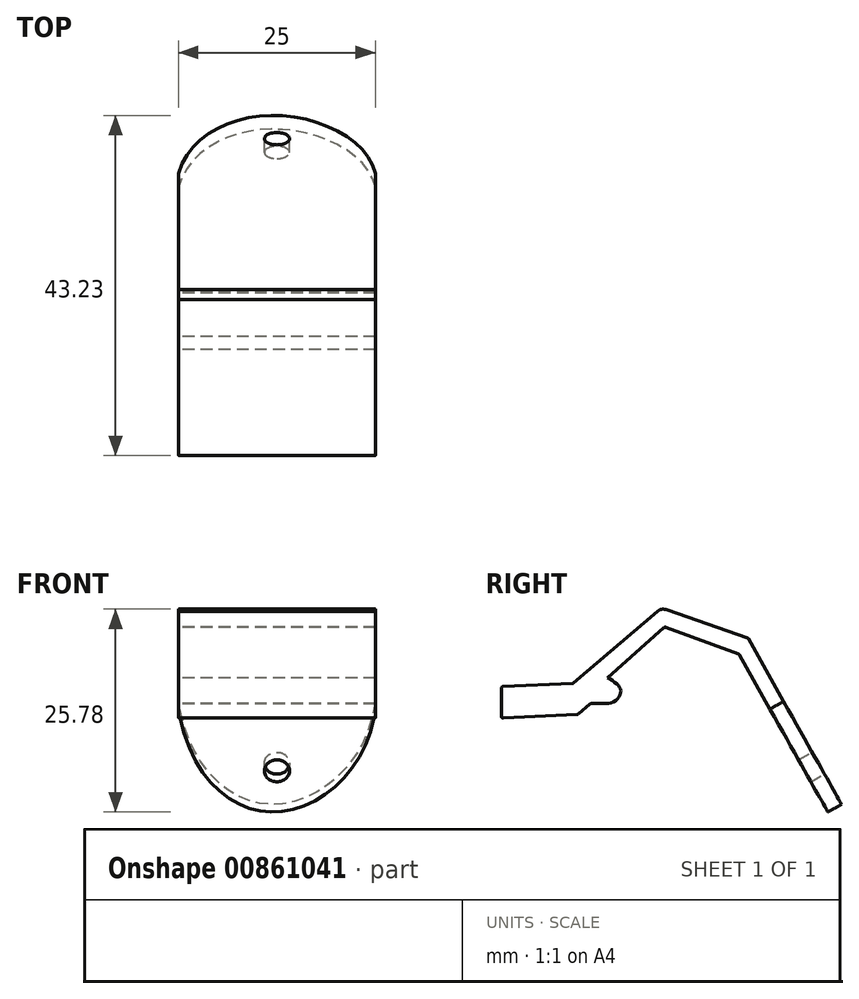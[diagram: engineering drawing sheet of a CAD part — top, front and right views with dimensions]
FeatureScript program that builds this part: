
annotation { "Feature Type Name" : "Feature", "Feature Type Description" : "" }
export const myFeature = defineFeature(function(context is Context, id is Id, definition is map)
    precondition{}
    {
        {
            var Q0;
            Q0=qCreatedBy(makeId("Right.planeOp"),FACE);
            var sketch = newSketch(context, id + "F0", { "sketchPlane" : qUnion([Q0])});
            skLineSegment(sketch, "E0", {"start": v(-12.97, -2.17) * mm, "end": v(-2.3, 6.93) * mm});
            skLineSegment(sketch, "E1", {"start": v(-1.03, 7.12) * mm, "end": v(9.1, 3.58) * mm});
            skLineSegment(sketch, "E2", {"start": v(11.98, -5.5) * mm, "end": v(8.12, 1.41) * mm});
            skLineSegment(sketch, "E3", {"start": v(8, 1.52) * mm, "end": v(-1.24, 4.91) * mm});
            skLineSegment(sketch, "E4", {"start": v(-1.48, 4.87) * mm, "end": v(-8.68, -1.5) * mm});
            skLineSegment(sketch, "E5", {"start": v(-13.1, -2.23) * mm, "end": v(-21.92, -2.62) * mm});
            skLineSegment(sketch, "E6", {"start": v(-22.14, -2.86) * mm, "end": v(-22.14, -6.38) * mm});
            skLineSegment(sketch, "E7", {"start": v(-21.9, -6.62) * mm, "end": v(-12.5, -6.17) * mm});
            skLineSegment(sketch, "E8", {"start": v(-12.36, -6.1) * mm, "end": v(-10.87, -4.84) * mm});
            skFitSpline(sketch, "E9", {"points": [v(-10.8, -4.79) * mm, v(-9.92, -4.79) * mm, v(-7.9, -4.56) * mm, v(-7.02, -3.54) * mm, v(-7.19, -2.58) * mm, v(-8.68, -1.5) * mm], "startDerivative": vector(3.35, 0.13) * mm, "endDerivative": vector(-7.8, 4.29) * mm});
            skLineSegment(sketch, "E10", {"start": v(13.72, -4.5) * mm, "end": v(9.22, 3.47) * mm});
            skPoint(sketch, "E11.visualSharp", {"position": v(9.18, 3.55) * mm});
            skArc(sketch, "E11.filletArc", {"start": v(9.22, 3.47) * mm, "mid": v(9.17, 3.54) * mm, "end": v(9.1, 3.58) * mm});
            skPoint(sketch, "E12.visualSharp", {"position": v(-13.03, -2.23) * mm});
            skArc(sketch, "E12.filletArc", {"start": v(-13.1, -2.23) * mm, "mid": v(-13.03, -2.21) * mm, "end": v(-12.97, -2.17) * mm});
            skPoint(sketch, "E13.visualSharp", {"position": v(-22.14, -2.63) * mm});
            skArc(sketch, "E13.filletArc", {"start": v(-21.92, -2.62) * mm, "mid": v(-22.08, -2.7) * mm, "end": v(-22.14, -2.86) * mm});
            skPoint(sketch, "E14.visualSharp", {"position": v(-22.14, -6.63) * mm});
            skArc(sketch, "E14.filletArc", {"start": v(-22.14, -6.38) * mm, "mid": v(-22.07, -6.55) * mm, "end": v(-21.9, -6.62) * mm});
            skPoint(sketch, "E15.visualSharp", {"position": v(-12.42, -6.16) * mm});
            skArc(sketch, "E15.filletArc", {"start": v(-12.5, -6.17) * mm, "mid": v(-12.43, -6.15) * mm, "end": v(-12.36, -6.1) * mm});
            skArc(sketch, "E16.filletArc", {"start": v(-10.72, -4.78) * mm, "mid": v(-10.8, -4.8) * mm, "end": v(-10.87, -4.84) * mm});
            skPoint(sketch, "E17.visualSharp", {"position": v(-1.31, 4.94) * mm});
            skArc(sketch, "E17.filletArc", {"start": v(-1.24, 4.91) * mm, "mid": v(-1.31, 4.93) * mm, "end": v(-1.38, 4.92) * mm});
            skPoint(sketch, "E18.visualSharp", {"position": v(8.07, 1.49) * mm});
            skArc(sketch, "E18.filletArc", {"start": v(8.12, 1.41) * mm, "mid": v(8.06, 1.48) * mm, "end": v(8, 1.52) * mm});
            skLineSegment(sketch, "E19", {"start": v(13.72, -4.5) * mm, "end": v(11.98, -5.5) * mm});
            skLineSegment(sketch, "E20", {"start": v(-1.48, 4.87) * mm, "end": v(-1.38, 4.92) * mm});
            skFitSpline(sketch, "E21", {"points": [v(-1.03, 7.12) * mm, v(-2.3, 6.93) * mm], "startDerivative": vector(-1.48, 0.47) * mm, "endDerivative": vector(-1, -1) * mm});
            skSolve(sketch);
        }
        {
            var Q0;
            Q0 = qSketchRegion(id + "F0", true);
            extrude(context, id + "F1", {"entities" : qUnion([Q0]), "depth" : 25 * mm, "offsetDistance" : 25 * mm});
        }
        {
            var Q0;
            Q0=makeQuery(id+"F1.opExtrude","SWEPT_FACE",FACE,{"disambiguationData":[OSD([sQuery(id+"F0.wireOp",EDGE,"E10")])]});
            var sketch = newSketch(context, id + "F2", { "sketchPlane" : qUnion([Q0])});
            skPoint(sketch, "E22", {"position": v(-12.5, -19.66) * mm});
            skCircle(sketch, "E23", {"center": v(-12.5, -19.66) * mm, "radius": 1.6 * mm});
            skLineSegment(sketch, "E24", {"start": v(-12.5, -19.66) * mm, "end": v(-12.5, -0.12) * mm, "construction": true});
            skFitSpline(sketch, "E25", {"points": [v(-25, -10.66) * mm, v(-12.5, -25.66) * mm, v(0, -10.66) * mm], "startDerivative": vector(5.67, -51.85) * mm, "endDerivative": vector(8.17, 59.62) * mm});
            skLineSegment(sketch, "E26", {"start": v(-25, -10.66) * mm, "end": v(0, -10.66) * mm});
            skSolve(sketch);
        }
        {
            var Q0;
            Q0 = qSketchRegion(id + "F2", true);
            extrude(context, id + "F3", {"entities" : qUnion([Q0]), "operationType" : NewBodyOperationType.ADD, "oppositeDirection" : true, "depth" : 2 * mm, "offsetDistance" : 25 * mm});
        }
    });
